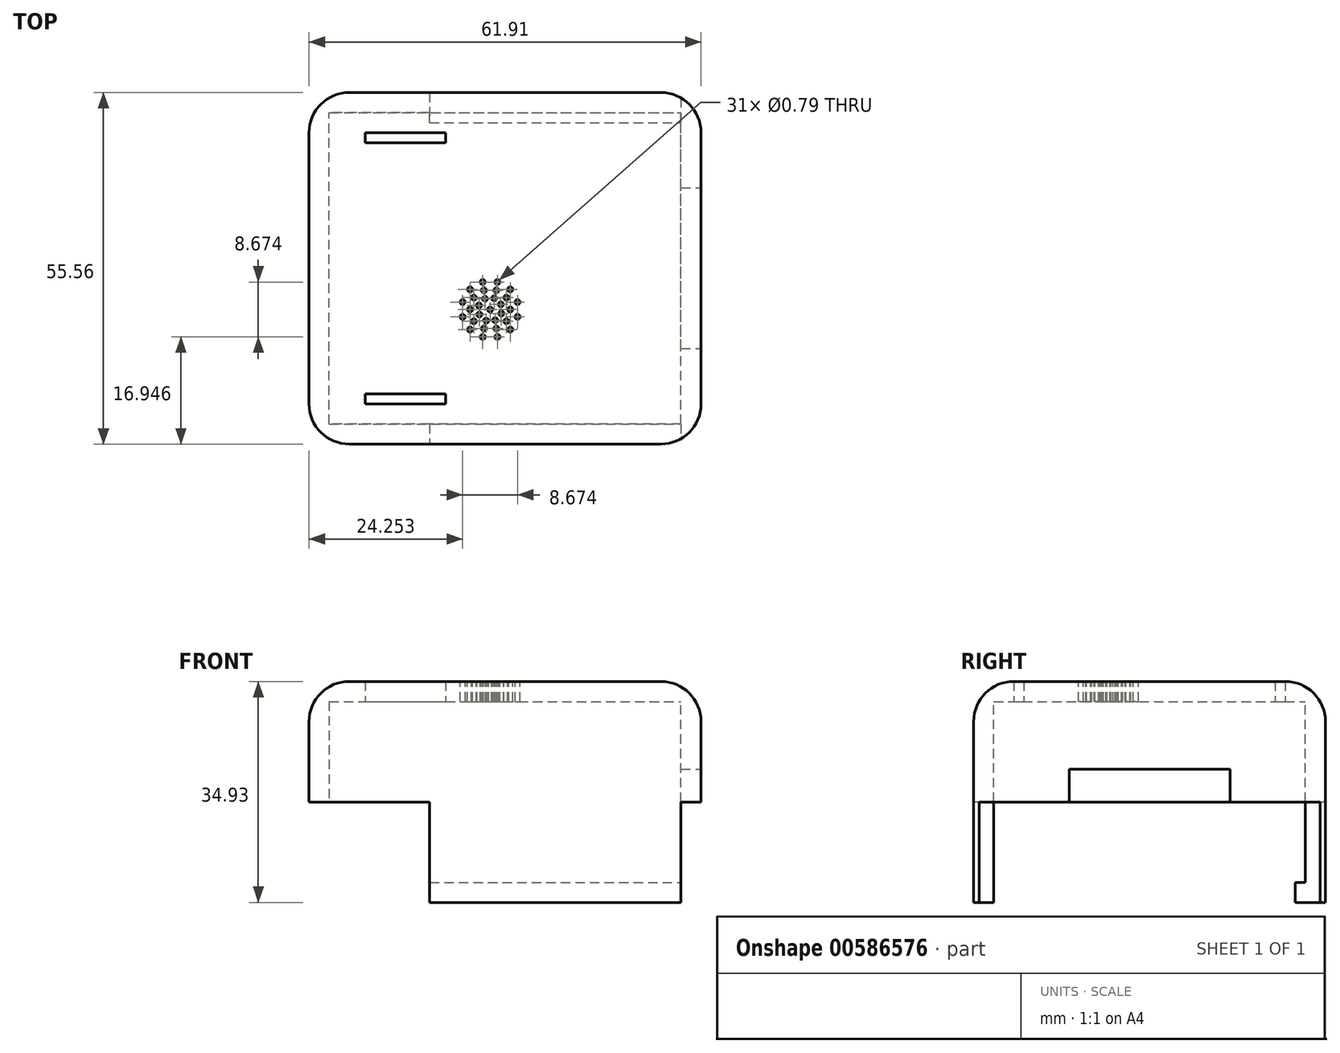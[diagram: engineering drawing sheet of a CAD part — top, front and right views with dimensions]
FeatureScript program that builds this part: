
annotation { "Feature Type Name" : "Feature", "Feature Type Description" : "" }
export const myFeature = defineFeature(function(context is Context, id is Id, definition is map)
    precondition{}
    {
        {
            var Q0;
            Q0=qCreatedBy(makeId("Top.planeOp"),FACE);
            var sketch = newSketch(context, id + "F0", { "sketchPlane" : qUnion([Q0])});
            skLineSegment(sketch, "E0.bottom", {"start": v(0, 0) * mm, "end": v(-61.91, 0) * mm});
            skLineSegment(sketch, "E0.top", {"start": v(0, 55.56) * mm, "end": v(-61.91, 55.56) * mm});
            skLineSegment(sketch, "E0.left", {"start": v(0, 0) * mm, "end": v(0, 55.56) * mm});
            skLineSegment(sketch, "E0.right", {"start": v(-61.91, 0) * mm, "end": v(-61.91, 55.56) * mm});
            skSolve(sketch);
        }
        {
            var Q0;
            Q0=makeQuery(id+"F0.imprint","IMPRINT",FACE,{"disambiguationData":[TD([[makeQuery(id+"F0.imprint","IMPRINT",EDGE,{"derivedFrom":sQuery(id+"F0.wireOp",EDGE,"E0.bottom")}),-1.0]])]});
            extrude(context, id + "F1", {"entities" : qUnion([Q0]), "depth" : 19.05 * mm, "offsetDistance" : 25.4 * mm});
        }
        {
            var Q0;
            Q0=makeQuery(id+"F1.opExtrude","SWEPT_FACE",FACE,{"disambiguationData":[OSD([sQuery(id+"F0.wireOp",EDGE,"E0.left")])]});
            var sketch = newSketch(context, id + "F2", { "sketchPlane" : qUnion([Q0])});
            skLineSegment(sketch, "E1.bottom", {"start": v(3.17, 15.88) * mm, "end": v(52.39, 15.88) * mm});
            skLineSegment(sketch, "E1.top", {"start": v(3.18, 0) * mm, "end": v(52.39, 0) * mm});
            skLineSegment(sketch, "E1.left", {"start": v(3.18, 15.88) * mm, "end": v(3.18, 0) * mm});
            skLineSegment(sketch, "E1.right", {"start": v(52.39, 15.88) * mm, "end": v(52.39, 0) * mm});
            skLineSegment(sketch, "E2", {"start": v(3.18, 27.04) * mm, "end": v(0, 27.04) * mm});
            skLineSegment(sketch, "E3", {"start": v(27.78, 15.88) * mm, "end": v(27.78, 19.05) * mm});
            skLineSegment(sketch, "E4", {"start": v(52.39, 25.25) * mm, "end": v(55.56, 25.25) * mm});
            skLineSegment(sketch, "E5", {"start": v(24.86, 0) * mm, "end": v(24.86, 0) * mm});
            skSolve(sketch);
        }
        {
            var Q0;
            {var subQ4=sQuery(id+"F2.wireOp",EDGE,"E1.top");Q0=makeQuery(id+"F2.imprint","IMPRINT",FACE,{"disambiguationData":[TD([[makeQuery(id+"F2.imprint","IMPRINT",EDGE,{"derivedFrom":subQ4}),1.0]])]});}
            extrude(context, id + "F3", {"entities" : qUnion([Q0]), "operationType" : NewBodyOperationType.REMOVE, "oppositeDirection" : true, "depth" : 58.74 * mm, "offsetDistance" : 25.4 * mm});
        }
        {
            var Q0;
            Q0=makeQuery(id+"F3.boolean.opBoolean","COPY",FACE,{"derivedFrom":makeQuery(id+"F3.opExtrude","SWEPT_FACE",FACE,{"disambiguationData":[OSD([sQuery(id+"F2.wireOp",EDGE,"E1.bottom")])]})});
            var sketch = newSketch(context, id + "F4", { "sketchPlane" : qUnion([Q0])});
            skLineSegment(sketch, "E6", {"start": v(0, -3.17) * mm, "end": v(-3.18, -3.17) * mm});
            skLineSegment(sketch, "E7", {"start": v(-3.18, -3.17) * mm, "end": v(-3.17, -52.39) * mm});
            skLineSegment(sketch, "E8", {"start": v(-3.17, -52.39) * mm, "end": v(0, -52.39) * mm});
            skSolve(sketch);
        }
        {
            var Q0;
            Q0=makeQuery(id+"F4.imprint","IMPRINT",FACE,{"disambiguationData":[TD([[makeQuery(id+"F4.imprint","IMPRINT",EDGE,{"derivedFrom":sQuery(id+"F4.wireOp",EDGE,"E6")}),-1.0]])]});
            extrude(context, id + "F5", {"entities" : qUnion([Q0]), "operationType" : NewBodyOperationType.ADD, "depth" : 15.88 * mm, "offsetDistance" : 25.4 * mm});
        }
        {
            var Q0;
            Q0=makeQuery(id+"F5.boolean.opBoolean","MERGE",FACE,{"derivedFrom":[makeQuery(id+"F1.opExtrude","CAP_FACE",FACE,{"disambiguationData":[OSD([sQuery(id+"F0.wireOp",EDGE,"E0.bottom"),sQuery(id+"F0.wireOp",EDGE,"E0.top"),sQuery(id+"F0.wireOp",EDGE,"E0.left"),sQuery(id+"F0.wireOp",EDGE,"E0.right")])],"isStart":true}),makeQuery(id+"F5.opExtrude","CAP_FACE",FACE,{"disambiguationData":[OSD([sQuery(id+"F2.wireOp",EDGE,"E1.bottom"),sQuery(id+"F4.wireOp",EDGE,"E6"),sQuery(id+"F4.wireOp",EDGE,"E7"),sQuery(id+"F4.wireOp",EDGE,"E8")])],"isStart":false})]});
            var sketch = newSketch(context, id + "F6", { "sketchPlane" : qUnion([Q0])});
            skLineSegment(sketch, "E9", {"start": v(-58.74, -3.17) * mm, "end": v(-61.91, -3.17) * mm});
            skLineSegment(sketch, "E10", {"start": v(-3.18, -3.18) * mm, "end": v(0, -3.18) * mm});
            skLineSegment(sketch, "E11", {"start": v(-58.74, -52.39) * mm, "end": v(-61.91, -52.39) * mm});
            skLineSegment(sketch, "E12", {"start": v(-3.18, -52.39) * mm, "end": v(0, -52.39) * mm});
            skSolve(sketch);
        }
        {
            var Q0;
            {var subQ5=sQuery(id+"F6.wireOp",EDGE,"E9");Q0=makeQuery(id+"F6.imprint","IMPRINT",FACE,{"disambiguationData":[TD([[makeQuery(id+"F6.imprint","IMPRINT",EDGE,{"derivedFrom":subQ5}),-1.0]])]});}
            extrude(context, id + "F7", {"entities" : qUnion([Q0]), "operationType" : NewBodyOperationType.ADD, "depth" : 15.88 * mm, "offsetDistance" : 25.4 * mm});
        }
        {
            var Q0;
            Q0=makeQuery(id+"F5.boolean.opBoolean","MERGE",FACE,{"derivedFrom":[makeQuery(id+"F1.opExtrude","CAP_FACE",FACE,{"disambiguationData":[OSD([sQuery(id+"F0.wireOp",EDGE,"E0.bottom"),sQuery(id+"F0.wireOp",EDGE,"E0.top"),sQuery(id+"F0.wireOp",EDGE,"E0.left"),sQuery(id+"F0.wireOp",EDGE,"E0.right")])],"isStart":true}),makeQuery(id+"F5.opExtrude","CAP_FACE",FACE,{"disambiguationData":[OSD([sQuery(id+"F2.wireOp",EDGE,"E1.bottom"),sQuery(id+"F4.wireOp",EDGE,"E6"),sQuery(id+"F4.wireOp",EDGE,"E7"),sQuery(id+"F4.wireOp",EDGE,"E8")])],"isStart":false})]});
            var sketch = newSketch(context, id + "F8", { "sketchPlane" : qUnion([Q0])});
            skLineSegment(sketch, "E13", {"start": v(-58.74, -52.39) * mm, "end": v(-61.91, -52.39) * mm});
            skLineSegment(sketch, "E14", {"start": v(-3.18, -52.39) * mm, "end": v(0, -52.39) * mm});
            skSolve(sketch);
        }
        {
            var Q0;
            {var subQ5=sQuery(id+"F8.wireOp",EDGE,"E13");Q0=makeQuery(id+"F8.imprint","IMPRINT",FACE,{"disambiguationData":[TD([[makeQuery(id+"F8.imprint","IMPRINT",EDGE,{"derivedFrom":subQ5}),1.0]])]});}
            extrude(context, id + "F9", {"entities" : qUnion([Q0]), "operationType" : NewBodyOperationType.ADD, "depth" : 15.88 * mm, "offsetDistance" : 25.4 * mm});
        }
        {
            var Q0;
            {var subQ0=sQuery(id+"F0.wireOp",EDGE,"E0.bottom");Q0=makeQuery(id+"F7.boolean.opBoolean","MERGE",FACE,{"derivedFrom":[makeQuery(id+"F1.opExtrude","SWEPT_FACE",FACE,{"disambiguationData":[OSD([subQ0])]}),makeQuery(id+"F7.opExtrude","SWEPT_FACE",FACE,{"disambiguationData":[OSD([subQ0])]})]});}
            var sketch = newSketch(context, id + "F10", { "sketchPlane" : qUnion([Q0])});
            skLineSegment(sketch, "E15", {"start": v(-3.17, -15.88) * mm, "end": v(-3.18, 0) * mm});
            skLineSegment(sketch, "E16", {"start": v(-3.18, 0) * mm, "end": v(0, 0) * mm});
            skLineSegment(sketch, "E17", {"start": v(-42.86, -15.88) * mm, "end": v(-61.91, -15.88) * mm});
            skLineSegment(sketch, "E18", {"start": v(-42.86, -15.88) * mm, "end": v(-42.86, 0) * mm});
            skLineSegment(sketch, "E19", {"start": v(-42.86, 0) * mm, "end": v(-61.91, 0) * mm});
            skLineSegment(sketch, "E20", {"start": v(-61.91, 0) * mm, "end": v(-61.91, -15.88) * mm});
            skSolve(sketch);
        }
        {
            var Q0;
            Q0=makeQuery(id+"F10.imprint","IMPRINT",FACE,{"disambiguationData":[TD([[makeQuery(id+"F10.imprint","IMPRINT",EDGE,{"derivedFrom":sQuery(id+"F10.wireOp",EDGE,"E17")}),-1.0]])]});
            var Q1;
            {var subQ0=sQuery(id+"F10.wireOp",EDGE,"E15");Q1=makeQuery(id+"F10.imprint","IMPRINT",FACE,{"disambiguationData":[TD([[makeQuery(id+"F10.imprint","IMPRINT",EDGE,{"derivedFrom":subQ0}),-1.0]])]});}
            extrude(context, id + "F11", {"entities" : qUnion([Q0, Q1]), "operationType" : NewBodyOperationType.REMOVE, "oppositeDirection" : true, "depth" : 101.6 * mm, "offsetDistance" : 25.4 * mm});
        }
        {
            var Q0;
            {var subQ0=sQuery(id+"F0.wireOp",EDGE,"E0.right");var subQ1=sQuery(id+"F0.wireOp",EDGE,"E0.bottom");Q0=makeQuery(id+"F7.boolean.opBoolean","MERGE",EDGE,{"derivedFrom":[makeQuery(id+"F1.opExtrude","SWEPT_EDGE",EDGE,{"disambiguationData":[OSD([subQ1,subQ0])]}),makeQuery(id+"F7.opExtrude","SWEPT_EDGE",EDGE,{"disambiguationData":[OSD([subQ1,subQ0])]})]});}
            var Q1;
            Q1=makeQuery(id+"F1.opExtrude","CAP_EDGE",EDGE,{"disambiguationData":[OSD([sQuery(id+"F0.wireOp",EDGE,"E0.bottom")])],"isStart":false});
            var Q2;
            Q2=makeQuery(id+"F1.opExtrude","CAP_EDGE",EDGE,{"disambiguationData":[OSD([sQuery(id+"F0.wireOp",EDGE,"E0.right")])],"isStart":false});
            var Q3;
            {var subQ0=sQuery(id+"F0.wireOp",EDGE,"E0.left");var subQ1=sQuery(id+"F0.wireOp",EDGE,"E0.bottom");Q3=makeQuery(id+"F7.boolean.opBoolean","MERGE",EDGE,{"derivedFrom":[makeQuery(id+"F1.opExtrude","SWEPT_EDGE",EDGE,{"disambiguationData":[OSD([subQ1,subQ0])]}),makeQuery(id+"F7.opExtrude","SWEPT_EDGE",EDGE,{"disambiguationData":[OSD([subQ1,subQ0,sQuery(id+"F2.wireOp",EDGE,"E1.bottom")])]})]});}
            var Q4;
            Q4=makeQuery(id+"F1.opExtrude","CAP_EDGE",EDGE,{"disambiguationData":[OSD([sQuery(id+"F0.wireOp",EDGE,"E0.left")])],"isStart":false});
            var Q5;
            {var subQ0=sQuery(id+"F0.wireOp",EDGE,"E0.left");var subQ1=sQuery(id+"F0.wireOp",EDGE,"E0.top");Q5=makeQuery(id+"F9.boolean.opBoolean","MERGE",EDGE,{"derivedFrom":[makeQuery(id+"F1.opExtrude","SWEPT_EDGE",EDGE,{"disambiguationData":[OSD([subQ1,subQ0])]}),makeQuery(id+"F9.opExtrude","SWEPT_EDGE",EDGE,{"disambiguationData":[OSD([subQ1,subQ0,sQuery(id+"F2.wireOp",EDGE,"E1.bottom")])]})]});}
            var Q6;
            {var subQ0=sQuery(id+"F0.wireOp",EDGE,"E0.right");var subQ1=sQuery(id+"F0.wireOp",EDGE,"E0.top");Q6=makeQuery(id+"F9.boolean.opBoolean","MERGE",EDGE,{"derivedFrom":[makeQuery(id+"F1.opExtrude","SWEPT_EDGE",EDGE,{"disambiguationData":[OSD([subQ1,subQ0])]}),makeQuery(id+"F9.opExtrude","SWEPT_EDGE",EDGE,{"disambiguationData":[OSD([subQ1,subQ0])]})]});}
            var Q7;
            Q7=makeQuery(id+"F1.opExtrude","CAP_FACE",FACE,{"disambiguationData":[OSD([sQuery(id+"F0.wireOp",EDGE,"E0.bottom"),sQuery(id+"F0.wireOp",EDGE,"E0.top"),sQuery(id+"F0.wireOp",EDGE,"E0.left"),sQuery(id+"F0.wireOp",EDGE,"E0.right")])],"isStart":false});
            fillet(context, id + "F12", {"entities" : qUnion([Q0, Q1, Q2, Q3, Q4, Q5, Q6, Q7]), "radius" : 6.35 * mm, "tangentPropagation" : true, "allowEdgeOverflow" : false});
        }
        {
            var Q0;
            {var subQ0=sQuery(id+"F2.wireOp",EDGE,"E1.bottom");var subQ1=sQuery(id+"F0.wireOp",EDGE,"E0.left");Q0=makeQuery(id+"F9.boolean.opBoolean","MERGE",FACE,{"derivedFrom":[makeQuery(id+"F7.boolean.opBoolean","MERGE",FACE,{"derivedFrom":[makeQuery(id+"F5.boolean.opBoolean","MERGE",FACE,{"derivedFrom":[makeQuery(id+"F1.opExtrude","SWEPT_FACE",FACE,{"disambiguationData":[OSD([subQ1])]}),makeQuery(id+"F5.opExtrude","SWEPT_FACE",FACE,{"disambiguationData":[OSD([subQ0])]})]}),makeQuery(id+"F7.opExtrude","SWEPT_FACE",FACE,{"disambiguationData":[OSD([subQ1,subQ0])]})]}),makeQuery(id+"F9.opExtrude","SWEPT_FACE",FACE,{"disambiguationData":[OSD([subQ1,subQ0])]})]});}
            var sketch = newSketch(context, id + "F13", { "sketchPlane" : qUnion([Q0])});
            skLineSegment(sketch, "E21", {"start": v(15.08, 0) * mm, "end": v(15.08, 5.16) * mm});
            skLineSegment(sketch, "E22", {"start": v(15.08, 5.16) * mm, "end": v(40.48, 5.16) * mm});
            skLineSegment(sketch, "E23", {"start": v(40.48, 5.16) * mm, "end": v(40.48, 0) * mm});
            skLineSegment(sketch, "E24", {"start": v(40.48, 0) * mm, "end": v(49.21, 0) * mm});
            skLineSegment(sketch, "E25", {"start": v(6.35, 0) * mm, "end": v(15.08, 0) * mm});
            skSolve(sketch);
        }
        {
            var Q0;
            {var subQ0=sQuery(id+"F13.wireOp",EDGE,"E21");Q0=makeQuery(id+"F13.imprint","IMPRINT",FACE,{"disambiguationData":[TD([[makeQuery(id+"F13.imprint","IMPRINT",EDGE,{"derivedFrom":subQ0}),-1.0]])]});}
            extrude(context, id + "F14", {"entities" : qUnion([Q0]), "operationType" : NewBodyOperationType.REMOVE, "oppositeDirection" : true, "depth" : 25.4 * mm, "offsetDistance" : 25.4 * mm});
        }
        {
            var Q0;
            Q0=makeQuery(id+"F3.boolean.opBoolean","COPY",FACE,{"derivedFrom":makeQuery(id+"F3.opExtrude","SWEPT_FACE",FACE,{"disambiguationData":[OSD([sQuery(id+"F2.wireOp",EDGE,"E1.bottom")])]})});
            var sketch = newSketch(context, id + "F15", { "sketchPlane" : qUnion([Q0])});
            skLineSegment(sketch, "E26.bottom", {"start": v(-53.06, -47.63) * mm, "end": v(-40.36, -47.63) * mm});
            skLineSegment(sketch, "E26.top", {"start": v(-53.06, -49.21) * mm, "end": v(-40.36, -49.21) * mm});
            skLineSegment(sketch, "E26.left", {"start": v(-53.06, -47.63) * mm, "end": v(-53.06, -49.21) * mm});
            skLineSegment(sketch, "E26.right", {"start": v(-40.36, -47.63) * mm, "end": v(-40.36, -49.21) * mm});
            skLineSegment(sketch, "E27.bottom", {"start": v(-53.06, -6.35) * mm, "end": v(-40.36, -6.35) * mm});
            skLineSegment(sketch, "E27.top", {"start": v(-53.06, -7.94) * mm, "end": v(-40.36, -7.94) * mm});
            skLineSegment(sketch, "E27.left", {"start": v(-53.06, -6.35) * mm, "end": v(-53.06, -7.94) * mm});
            skLineSegment(sketch, "E27.right", {"start": v(-40.36, -6.35) * mm, "end": v(-40.36, -7.94) * mm});
            skLineSegment(sketch, "E28", {"start": v(-46.71, -6.35) * mm, "end": v(-46.71, -3.17) * mm});
            skLineSegment(sketch, "E29", {"start": v(-46.71, -49.21) * mm, "end": v(-46.71, -52.39) * mm});
            skSolve(sketch);
        }
        {
            var Q0;
            Q0=makeQuery(id+"F15.imprint","IMPRINT",FACE,{"disambiguationData":[TD([[makeQuery(id+"F15.imprint","IMPRINT",EDGE,{"derivedFrom":sQuery(id+"F15.wireOp",EDGE,"E27.top")}),1.0]])]});
            var Q1;
            Q1=makeQuery(id+"F15.imprint","IMPRINT",FACE,{"disambiguationData":[TD([[makeQuery(id+"F15.imprint","IMPRINT",EDGE,{"derivedFrom":sQuery(id+"F15.wireOp",EDGE,"E26.bottom")}),-1.0]])]});
            extrude(context, id + "F16", {"entities" : qUnion([Q0, Q1]), "operationType" : NewBodyOperationType.REMOVE, "oppositeDirection" : true, "depth" : 25.4 * mm, "offsetDistance" : 25.4 * mm});
        }
        {
            var Q0;
            {var subQ0=sQuery(id+"F2.wireOp",EDGE,"E1.right");Q0=makeQuery(id+"F9.boolean.opBoolean","MERGE",FACE,{"derivedFrom":[makeQuery(id+"F3.boolean.opBoolean","COPY",FACE,{"derivedFrom":makeQuery(id+"F3.opExtrude","SWEPT_FACE",FACE,{"disambiguationData":[OSD([subQ0])]})}),makeQuery(id+"F9.opExtrude","SWEPT_FACE",FACE,{"disambiguationData":[OSD([sQuery(id+"F0.wireOp",EDGE,"E0.left"),sQuery(id+"F2.wireOp",EDGE,"E1.top"),subQ0,sQuery(id+"F8.wireOp",EDGE,"E13"),sQuery(id+"F8.wireOp",EDGE,"E14")])]})]});}
            var sketch = newSketch(context, id + "F17", { "sketchPlane" : qUnion([Q0])});
            skLineSegment(sketch, "E30.bottom", {"start": v(-42.86, -15.88) * mm, "end": v(-3.17, -15.88) * mm});
            skLineSegment(sketch, "E30.top", {"start": v(-42.86, -12.7) * mm, "end": v(-3.17, -12.7) * mm});
            skLineSegment(sketch, "E30.left", {"start": v(-42.86, -15.88) * mm, "end": v(-42.86, -12.7) * mm});
            skLineSegment(sketch, "E30.right", {"start": v(-3.17, -15.88) * mm, "end": v(-3.17, -12.7) * mm});
            skSolve(sketch);
        }
        {
            var Q0;
            Q0=makeQuery(id+"F17.imprint","IMPRINT",FACE,{"disambiguationData":[TD([[makeQuery(id+"F17.imprint","IMPRINT",EDGE,{"derivedFrom":sQuery(id+"F17.wireOp",EDGE,"E30.bottom")}),1.0]])]});
            extrude(context, id + "F18", {"entities" : qUnion([Q0]), "operationType" : NewBodyOperationType.ADD, "depth" : 1.59 * mm, "offsetDistance" : 25.4 * mm});
        }
        {
            var Q0;
            Q0=makeQuery(id+"F1.opExtrude","CAP_FACE",FACE,{"disambiguationData":[OSD([sQuery(id+"F0.wireOp",EDGE,"E0.bottom"),sQuery(id+"F0.wireOp",EDGE,"E0.top"),sQuery(id+"F0.wireOp",EDGE,"E0.left"),sQuery(id+"F0.wireOp",EDGE,"E0.right")])],"isStart":false});
            var sketch = newSketch(context, id + "F19", { "sketchPlane" : qUnion([Q0])});
            skLineSegment(sketch, "E31", {"start": v(-6.35, 21.28) * mm, "end": v(-55.56, 21.28) * mm});
            skLineSegment(sketch, "E32", {"start": v(-33.32, 49.21) * mm, "end": v(-33.32, 6.35) * mm});
            skPoint(sketch, "E33.center", {"position": v(-33.32, 21.28) * mm});
            skCircle(sketch, "E34", {"center": v(-36.5, 24.46) * mm, "radius": 0.4 * mm});
            skCircle(sketch, "E35", {"center": v(-33.32, 21.28) * mm, "radius": 0.4 * mm});
            skLineSegment(sketch, "E36", {"start": v(-36.5, 24.46) * mm, "end": v(-36.5, 21.28) * mm});
            skLineSegment(sketch, "E37", {"start": v(-36.5, 24.46) * mm, "end": v(-33.32, 24.46) * mm});
            skCircle(sketch, "E38.1.0", {"center": v(-37.66, 22.45) * mm, "radius": 0.4 * mm});
            skCircle(sketch, "E38.2.0", {"center": v(-37.66, 20.12) * mm, "radius": 0.4 * mm});
            skCircle(sketch, "E38.3.0", {"center": v(-36.5, 18.1) * mm, "radius": 0.4 * mm});
            skCircle(sketch, "E38.4.0", {"center": v(-34.48, 16.95) * mm, "radius": 0.4 * mm});
            skCircle(sketch, "E38.5.0", {"center": v(-32.16, 16.95) * mm, "radius": 0.4 * mm});
            skCircle(sketch, "E38.6.0", {"center": v(-30.15, 18.1) * mm, "radius": 0.4 * mm});
            skCircle(sketch, "E38.7.0", {"center": v(-28.98, 20.12) * mm, "radius": 0.4 * mm});
            skCircle(sketch, "E38.8.0", {"center": v(-28.98, 22.45) * mm, "radius": 0.4 * mm});
            skCircle(sketch, "E38.9.0", {"center": v(-30.15, 24.46) * mm, "radius": 0.4 * mm});
            skCircle(sketch, "E38.10.0", {"center": v(-32.16, 25.62) * mm, "radius": 0.4 * mm});
            skCircle(sketch, "E38.11.0", {"center": v(-34.48, 25.62) * mm, "radius": 0.4 * mm});
            skCircle(sketch, "E39", {"center": v(-36.5, 21.28) * mm, "radius": 0.4 * mm});
            skCircle(sketch, "E40.1.0", {"center": v(-35.89, 19.42) * mm, "radius": 0.4 * mm});
            skCircle(sketch, "E40.2.0", {"center": v(-34.3, 18.26) * mm, "radius": 0.4 * mm});
            skCircle(sketch, "E40.3.0", {"center": v(-32.34, 18.26) * mm, "radius": 0.4 * mm});
            skCircle(sketch, "E40.4.0", {"center": v(-30.75, 19.42) * mm, "radius": 0.4 * mm});
            skCircle(sketch, "E40.5.0", {"center": v(-30.15, 21.28) * mm, "radius": 0.4 * mm});
            skCircle(sketch, "E40.6.0", {"center": v(-30.75, 23.15) * mm, "radius": 0.4 * mm});
            skCircle(sketch, "E40.7.0", {"center": v(-32.34, 24.3) * mm, "radius": 0.4 * mm});
            skCircle(sketch, "E40.8.0", {"center": v(-34.3, 24.3) * mm, "radius": 0.4 * mm});
            skCircle(sketch, "E40.9.0", {"center": v(-35.89, 23.15) * mm, "radius": 0.4 * mm});
            skCircle(sketch, "E41", {"center": v(-34.12, 22.98) * mm, "radius": 0.4 * mm});
            skLineSegment(sketch, "E42", {"start": v(-34.12, 22.98) * mm, "end": v(-33.32, 22.98) * mm});
            skLineSegment(sketch, "E43", {"start": v(-34.12, 22.98) * mm, "end": v(-34.12, 21.28) * mm});
            skCircle(sketch, "E44.1.0", {"center": v(-35.09, 21.92) * mm, "radius": 0.4 * mm});
            skCircle(sketch, "E44.2.0", {"center": v(-35.02, 20.48) * mm, "radius": 0.4 * mm});
            skCircle(sketch, "E44.3.0", {"center": v(-33.96, 19.52) * mm, "radius": 0.4 * mm});
            skCircle(sketch, "E44.4.0", {"center": v(-32.52, 19.58) * mm, "radius": 0.4 * mm});
            skCircle(sketch, "E44.5.0", {"center": v(-31.55, 20.65) * mm, "radius": 0.4 * mm});
            skCircle(sketch, "E44.6.0", {"center": v(-31.62, 22.08) * mm, "radius": 0.4 * mm});
            skCircle(sketch, "E44.7.0", {"center": v(-32.68, 23.05) * mm, "radius": 0.4 * mm});
            skSolve(sketch);
        }
        {
            var Q0;
            {var subQ0=sQuery(id+"F19.wireOp",EDGE,"E36");var subQ1=sQuery(id+"F19.wireOp",EDGE,"E34");var subQ2=makeQuery(id+"F19.imprint","INTERSECT",VERTEX,{"derivedFrom":[subQ1,subQ0]});Q0=makeQuery(id+"F19.imprint","IMPRINT",FACE,{"disambiguationData":[TD([[makeQuery(id+"F19.imprint","IMPRINT",EDGE,{"disambiguationData":[TD([[subQ2,1.0]])],"derivedFrom":subQ1}),1.0]])]});}
            var Q1;
            {var subQ0=sQuery(id+"F19.wireOp",EDGE,"E36");var subQ1=sQuery(id+"F19.wireOp",EDGE,"E34");var subQ2=makeQuery(id+"F19.imprint","INTERSECT",VERTEX,{"derivedFrom":[subQ1,subQ0]});Q1=makeQuery(id+"F19.imprint","IMPRINT",FACE,{"disambiguationData":[TD([[makeQuery(id+"F19.imprint","IMPRINT",EDGE,{"disambiguationData":[TD([[subQ2,-1.0]])],"derivedFrom":subQ1}),1.0]])]});}
            var Q2;
            Q2=makeQuery(id+"F19.imprint","IMPRINT",FACE,{"disambiguationData":[TD([[makeQuery(id+"F19.imprint","IMPRINT",EDGE,{"derivedFrom":sQuery(id+"F19.wireOp",EDGE,"E38.11.0")}),1.0]])]});
            var Q3;
            Q3=makeQuery(id+"F19.imprint","IMPRINT",FACE,{"disambiguationData":[TD([[makeQuery(id+"F19.imprint","IMPRINT",EDGE,{"derivedFrom":sQuery(id+"F19.wireOp",EDGE,"E38.10.0")}),1.0]])]});
            var Q4;
            Q4=makeQuery(id+"F19.imprint","IMPRINT",FACE,{"disambiguationData":[TD([[makeQuery(id+"F19.imprint","IMPRINT",EDGE,{"derivedFrom":sQuery(id+"F19.wireOp",EDGE,"E38.9.0")}),1.0]])]});
            var Q5;
            Q5=makeQuery(id+"F19.imprint","IMPRINT",FACE,{"disambiguationData":[TD([[makeQuery(id+"F19.imprint","IMPRINT",EDGE,{"derivedFrom":sQuery(id+"F19.wireOp",EDGE,"E38.8.0")}),1.0]])]});
            var Q6;
            Q6=makeQuery(id+"F19.imprint","IMPRINT",FACE,{"disambiguationData":[TD([[makeQuery(id+"F19.imprint","IMPRINT",EDGE,{"derivedFrom":sQuery(id+"F19.wireOp",EDGE,"E38.7.0")}),1.0]])]});
            var Q7;
            Q7=makeQuery(id+"F19.imprint","IMPRINT",FACE,{"disambiguationData":[TD([[makeQuery(id+"F19.imprint","IMPRINT",EDGE,{"derivedFrom":sQuery(id+"F19.wireOp",EDGE,"E38.6.0")}),1.0]])]});
            var Q8;
            Q8=makeQuery(id+"F19.imprint","IMPRINT",FACE,{"disambiguationData":[TD([[makeQuery(id+"F19.imprint","IMPRINT",EDGE,{"derivedFrom":sQuery(id+"F19.wireOp",EDGE,"E38.5.0")}),1.0]])]});
            var Q9;
            Q9=makeQuery(id+"F19.imprint","IMPRINT",FACE,{"disambiguationData":[TD([[makeQuery(id+"F19.imprint","IMPRINT",EDGE,{"derivedFrom":sQuery(id+"F19.wireOp",EDGE,"E40.3.0")}),1.0]])]});
            var Q10;
            Q10=makeQuery(id+"F19.imprint","IMPRINT",FACE,{"disambiguationData":[TD([[makeQuery(id+"F19.imprint","IMPRINT",EDGE,{"derivedFrom":sQuery(id+"F19.wireOp",EDGE,"E40.4.0")}),1.0]])]});
            var Q11;
            {var subQ0=sQuery(id+"F19.wireOp",EDGE,"E40.5.0");var subQ1=sQuery(id+"F19.wireOp",EDGE,"E31");var subQ2=makeQuery(id+"F19.imprint","INTERSECT",VERTEX,{"disambiguationData":[OD(0.0)],"derivedFrom":[subQ1,subQ0]});Q11=makeQuery(id+"F19.imprint","IMPRINT",FACE,{"disambiguationData":[TD([[makeQuery(id+"F19.imprint","IMPRINT",EDGE,{"disambiguationData":[TD([[subQ2,-1.0]])],"derivedFrom":subQ1}),1.0]])]});}
            var Q12;
            Q12=makeQuery(id+"F19.imprint","IMPRINT",FACE,{"disambiguationData":[TD([[makeQuery(id+"F19.imprint","IMPRINT",EDGE,{"derivedFrom":sQuery(id+"F19.wireOp",EDGE,"E44.5.0")}),1.0]])]});
            var Q13;
            Q13=makeQuery(id+"F19.imprint","IMPRINT",FACE,{"disambiguationData":[TD([[makeQuery(id+"F19.imprint","IMPRINT",EDGE,{"derivedFrom":sQuery(id+"F19.wireOp",EDGE,"E44.4.0")}),1.0]])]});
            var Q14;
            {var subQ0=sQuery(id+"F19.wireOp",EDGE,"E35");var subQ1=sQuery(id+"F19.wireOp",EDGE,"E31");var subQ2=makeQuery(id+"F19.imprint","INTERSECT",VERTEX,{"disambiguationData":[OD(0.0)],"derivedFrom":[subQ1,subQ0]});Q14=makeQuery(id+"F19.imprint","IMPRINT",FACE,{"disambiguationData":[TD([[makeQuery(id+"F19.imprint","IMPRINT",EDGE,{"disambiguationData":[TD([[subQ2,-1.0]])],"derivedFrom":subQ1}),1.0]])]});}
            var Q15;
            {var subQ0=sQuery(id+"F19.wireOp",EDGE,"E40.5.0");var subQ1=sQuery(id+"F19.wireOp",EDGE,"E31");var subQ2=makeQuery(id+"F19.imprint","INTERSECT",VERTEX,{"disambiguationData":[OD(0.0)],"derivedFrom":[subQ1,subQ0]});Q15=makeQuery(id+"F19.imprint","IMPRINT",FACE,{"disambiguationData":[TD([[makeQuery(id+"F19.imprint","IMPRINT",EDGE,{"disambiguationData":[TD([[subQ2,-1.0]])],"derivedFrom":subQ1}),-1.0]])]});}
            var Q16;
            Q16=makeQuery(id+"F19.imprint","IMPRINT",FACE,{"disambiguationData":[TD([[makeQuery(id+"F19.imprint","IMPRINT",EDGE,{"derivedFrom":sQuery(id+"F19.wireOp",EDGE,"E44.6.0")}),1.0]])]});
            var Q17;
            {var subQ0=sQuery(id+"F19.wireOp",EDGE,"E35");var subQ1=sQuery(id+"F19.wireOp",EDGE,"E31");var subQ2=makeQuery(id+"F19.imprint","INTERSECT",VERTEX,{"disambiguationData":[OD(0.0)],"derivedFrom":[subQ1,subQ0]});Q17=makeQuery(id+"F19.imprint","IMPRINT",FACE,{"disambiguationData":[TD([[makeQuery(id+"F19.imprint","IMPRINT",EDGE,{"disambiguationData":[TD([[subQ2,-1.0]])],"derivedFrom":subQ1}),-1.0]])]});}
            var Q18;
            Q18=makeQuery(id+"F19.imprint","IMPRINT",FACE,{"disambiguationData":[TD([[makeQuery(id+"F19.imprint","IMPRINT",EDGE,{"derivedFrom":sQuery(id+"F19.wireOp",EDGE,"E44.7.0")}),1.0]])]});
            var Q19;
            Q19=makeQuery(id+"F19.imprint","IMPRINT",FACE,{"disambiguationData":[TD([[makeQuery(id+"F19.imprint","IMPRINT",EDGE,{"derivedFrom":sQuery(id+"F19.wireOp",EDGE,"E40.7.0")}),1.0]])]});
            var Q20;
            Q20=makeQuery(id+"F19.imprint","IMPRINT",FACE,{"disambiguationData":[TD([[makeQuery(id+"F19.imprint","IMPRINT",EDGE,{"derivedFrom":sQuery(id+"F19.wireOp",EDGE,"E40.6.0")}),1.0]])]});
            var Q21;
            {var subQ0=sQuery(id+"F19.wireOp",EDGE,"E42");var subQ1=sQuery(id+"F19.wireOp",EDGE,"E41");var subQ2=makeQuery(id+"F19.imprint","INTERSECT",VERTEX,{"derivedFrom":[subQ1,subQ0]});Q21=makeQuery(id+"F19.imprint","IMPRINT",FACE,{"disambiguationData":[TD([[makeQuery(id+"F19.imprint","IMPRINT",EDGE,{"disambiguationData":[TD([[subQ2,-1.0]])],"derivedFrom":subQ1}),1.0]])]});}
            var Q22;
            {var subQ0=sQuery(id+"F19.wireOp",EDGE,"E42");var subQ1=sQuery(id+"F19.wireOp",EDGE,"E41");var subQ2=makeQuery(id+"F19.imprint","INTERSECT",VERTEX,{"derivedFrom":[subQ1,subQ0]});Q22=makeQuery(id+"F19.imprint","IMPRINT",FACE,{"disambiguationData":[TD([[makeQuery(id+"F19.imprint","IMPRINT",EDGE,{"disambiguationData":[TD([[subQ2,1.0]])],"derivedFrom":subQ1}),1.0]])]});}
            var Q23;
            {var subQ0=sQuery(id+"F19.wireOp",EDGE,"E40.8.0");var subQ1=sQuery(id+"F19.wireOp",EDGE,"E37");var subQ2=makeQuery(id+"F19.imprint","INTERSECT",VERTEX,{"disambiguationData":[OD(0.0)],"derivedFrom":[subQ1,subQ0]});Q23=makeQuery(id+"F19.imprint","IMPRINT",FACE,{"disambiguationData":[TD([[makeQuery(id+"F19.imprint","IMPRINT",EDGE,{"disambiguationData":[TD([[subQ2,-1.0]])],"derivedFrom":subQ1}),-1.0]])]});}
            var Q24;
            {var subQ0=sQuery(id+"F19.wireOp",EDGE,"E40.8.0");var subQ1=sQuery(id+"F19.wireOp",EDGE,"E37");var subQ2=makeQuery(id+"F19.imprint","INTERSECT",VERTEX,{"disambiguationData":[OD(0.0)],"derivedFrom":[subQ1,subQ0]});Q24=makeQuery(id+"F19.imprint","IMPRINT",FACE,{"disambiguationData":[TD([[makeQuery(id+"F19.imprint","IMPRINT",EDGE,{"disambiguationData":[TD([[subQ2,-1.0]])],"derivedFrom":subQ1}),1.0]])]});}
            var Q25;
            Q25=makeQuery(id+"F19.imprint","IMPRINT",FACE,{"disambiguationData":[TD([[makeQuery(id+"F19.imprint","IMPRINT",EDGE,{"derivedFrom":sQuery(id+"F19.wireOp",EDGE,"E40.9.0")}),1.0]])]});
            var Q26;
            Q26=makeQuery(id+"F19.imprint","IMPRINT",FACE,{"disambiguationData":[TD([[makeQuery(id+"F19.imprint","IMPRINT",EDGE,{"derivedFrom":sQuery(id+"F19.wireOp",EDGE,"E44.1.0")}),1.0]])]});
            var Q27;
            {var subQ0=sQuery(id+"F19.wireOp",EDGE,"E32");var subQ1=sQuery(id+"F19.wireOp",EDGE,"E31");var subQ2=makeQuery(id+"F19.imprint","INTERSECT",VERTEX,{"derivedFrom":[subQ1,subQ0]});Q27=makeQuery(id+"F19.imprint","IMPRINT",FACE,{"disambiguationData":[TD([[makeQuery(id+"F19.imprint","IMPRINT",EDGE,{"disambiguationData":[TD([[subQ2,-1.0]])],"derivedFrom":subQ1}),-1.0]])]});}
            var Q28;
            {var subQ0=sQuery(id+"F19.wireOp",EDGE,"E36");var subQ1=sQuery(id+"F19.wireOp",EDGE,"E31");var subQ2=makeQuery(id+"F19.imprint","INTERSECT",VERTEX,{"derivedFrom":[subQ1,subQ0]});Q28=makeQuery(id+"F19.imprint","IMPRINT",FACE,{"disambiguationData":[TD([[makeQuery(id+"F19.imprint","IMPRINT",EDGE,{"disambiguationData":[TD([[subQ2,1.0]])],"derivedFrom":subQ1}),-1.0]])]});}
            var Q29;
            {var subQ0=sQuery(id+"F19.wireOp",EDGE,"E36");var subQ1=sQuery(id+"F19.wireOp",EDGE,"E31");var subQ2=makeQuery(id+"F19.imprint","INTERSECT",VERTEX,{"derivedFrom":[subQ1,subQ0]});Q29=makeQuery(id+"F19.imprint","IMPRINT",FACE,{"disambiguationData":[TD([[makeQuery(id+"F19.imprint","IMPRINT",EDGE,{"disambiguationData":[TD([[subQ2,-1.0]])],"derivedFrom":subQ1}),-1.0]])]});}
            var Q30;
            Q30=makeQuery(id+"F19.imprint","IMPRINT",FACE,{"disambiguationData":[TD([[makeQuery(id+"F19.imprint","IMPRINT",EDGE,{"derivedFrom":sQuery(id+"F19.wireOp",EDGE,"E38.1.0")}),1.0]])]});
            var Q31;
            Q31=makeQuery(id+"F19.imprint","IMPRINT",FACE,{"disambiguationData":[TD([[makeQuery(id+"F19.imprint","IMPRINT",EDGE,{"derivedFrom":sQuery(id+"F19.wireOp",EDGE,"E38.2.0")}),1.0]])]});
            var Q32;
            {var subQ0=sQuery(id+"F19.wireOp",EDGE,"E31");var subQ1=makeQuery(id+"F19.imprint","INTERSECT",VERTEX,{"derivedFrom":[subQ0,sQuery(id+"F19.wireOp",EDGE,"E36")]});Q32=makeQuery(id+"F19.imprint","IMPRINT",FACE,{"disambiguationData":[TD([[makeQuery(id+"F19.imprint","IMPRINT",EDGE,{"disambiguationData":[TD([[subQ1,1.0]])],"derivedFrom":subQ0}),1.0]])]});}
            var Q33;
            Q33=makeQuery(id+"F19.imprint","IMPRINT",FACE,{"disambiguationData":[TD([[makeQuery(id+"F19.imprint","IMPRINT",EDGE,{"derivedFrom":sQuery(id+"F19.wireOp",EDGE,"E44.2.0")}),1.0]])]});
            var Q34;
            Q34=makeQuery(id+"F19.imprint","IMPRINT",FACE,{"disambiguationData":[TD([[makeQuery(id+"F19.imprint","IMPRINT",EDGE,{"derivedFrom":sQuery(id+"F19.wireOp",EDGE,"E40.1.0")}),1.0]])]});
            var Q35;
            Q35=makeQuery(id+"F19.imprint","IMPRINT",FACE,{"disambiguationData":[TD([[makeQuery(id+"F19.imprint","IMPRINT",EDGE,{"derivedFrom":sQuery(id+"F19.wireOp",EDGE,"E38.3.0")}),1.0]])]});
            var Q36;
            Q36=makeQuery(id+"F19.imprint","IMPRINT",FACE,{"disambiguationData":[TD([[makeQuery(id+"F19.imprint","IMPRINT",EDGE,{"derivedFrom":sQuery(id+"F19.wireOp",EDGE,"E38.4.0")}),1.0]])]});
            var Q37;
            Q37=makeQuery(id+"F19.imprint","IMPRINT",FACE,{"disambiguationData":[TD([[makeQuery(id+"F19.imprint","IMPRINT",EDGE,{"derivedFrom":sQuery(id+"F19.wireOp",EDGE,"E40.2.0")}),1.0]])]});
            var Q38;
            Q38=makeQuery(id+"F19.imprint","IMPRINT",FACE,{"disambiguationData":[TD([[makeQuery(id+"F19.imprint","IMPRINT",EDGE,{"derivedFrom":sQuery(id+"F19.wireOp",EDGE,"E44.3.0")}),1.0]])]});
            var Q39;
            {var subQ0=sQuery(id+"F19.wireOp",EDGE,"E32");var subQ1=sQuery(id+"F19.wireOp",EDGE,"E31");var subQ2=makeQuery(id+"F19.imprint","INTERSECT",VERTEX,{"derivedFrom":[subQ1,subQ0]});Q39=makeQuery(id+"F19.imprint","IMPRINT",FACE,{"disambiguationData":[TD([[makeQuery(id+"F19.imprint","IMPRINT",EDGE,{"disambiguationData":[TD([[subQ2,-1.0]])],"derivedFrom":subQ1}),1.0]])]});}
            extrude(context, id + "F20", {"entities" : qUnion([Q0, Q1, Q2, Q3, Q4, Q5, Q6, Q7, Q8, Q9, Q10, Q11, Q12, Q13, Q14, Q15, Q16, Q17, Q18, Q19, Q20, Q21, Q22, Q23, Q24, Q25, Q26, Q27, Q28, Q29, Q30, Q31, Q32, Q33, Q34, Q35, Q36, Q37, Q38, Q39]), "operationType" : NewBodyOperationType.REMOVE, "oppositeDirection" : true, "depth" : 25.4 * mm, "offsetDistance" : 25.4 * mm});
        }
    });
